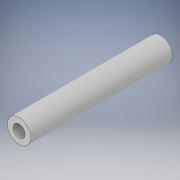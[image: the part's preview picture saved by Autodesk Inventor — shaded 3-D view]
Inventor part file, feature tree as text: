
AUTODESK INVENTOR PART (.ipt)
format: ipt  version: 2017 (Build 210142000, 142)  size: 92,672 bytes
history: native  units: in
note: dims shown in document units (in); Inventor stores cm internally (conversion verified against a paired STEP export)
features: extrude x1, sketch x1
ambient origin geometry x8: Origin, YZ Plane, XZ Plane, XY Plane, X Axis, Y Axis, Z Axis, Center Point
bodies: Solid1 (feature_tree)
feature tree (2):
  extrude  "Extrusion1"  [1 undecoded]
  sketch  "Sketch1"  dims[d0=3.0in d1=0.0in]
note: 1 required parameter value undecoded (feature->parameter linkage not recoverable at this tier; creation-order binding heuristic only, values carry confidence <= 0.55)
